# Revit family: ASafe_ASafeHQLtd_HndrlSym_iFlexPedestrianBarrier3Rail
name_source: partatom
category: Railings
revit_build: Autodesk Revit 2018 (Build: 20170223_1515(x64)
units: mm (PartAtom-declared; Revit-internal decimal feet)

## family parameters
Always vertical = No
Cut with Voids When Loaded = No
Shared = No
Work Plane-Based = Yes

## types (8) — shared parameters
AssetType = Fixed
BarrierColour = ASafe_ASafeHQLtd_Memaplex_SignalYellow
BasePlateSize = 180 x 180 mm
BaseplateMaterial = ASafe_ASafeHQLtd_SteelEcoCoating_Black
Category = Ss_25_15_60_35:Handrail systems
ChemicalResistance = Excellent - ISO/TR 10358
Color = Signal yellow
Constituents = Locking pins, Couplings with covers, Fixings
Default Elevation = 1219 mm
Deflection = 320 mm at maximum energy
DurationUnit = year
Duty = Light
FlashPoint = 350°C to 370°C
HandrailHeight = 1050 mm  [stored 3.44488 ft]
HasHygieneSeals = Yes
Height = 1136 mm
IfcExportAs = IfcRailingType
IfcExportType = USERDEFINED
IgnitionTemperature = 350°C to 370°C
ImpactJoules = Dynamically tested to resist an impact of 8,200 Joules from a vehicle impact at 45°
ImpactZone = 450-1100 mm
IsExternal = Yes
LiftingForce = 9 kN
ManufacturerName = A-Safe (HQ) Ltd
ManufacturerURL = https://www.asafe.com
Material = Memaplex
ModelReference = iFlex™ Pedestrian Barrier 3 Rail
MouldColour = ASafe_ASafeHQLtd_Memaplex_SignalYellow
MountingType = Floor fixed
NBSCertification = www.nationalbimlibrary.com/cert/vatznaso
NBSDescription = Handrail system
NBSReference = 25-25-10/135
NominalHeight = 1136 mm
NominalWidth = 130 mm
PostColour = ASafe_ASafeHQLtd_Memaplex_Black
PostHeight = 1136 mm
ProductInformation = https://www.asafe.com
StaticRating = 1015-1016 Ω
Status = UNSET
TemperatureRange = -10°C to 50°C
ThirdPartyCertification = PAS13:2017,TÜV NORD Approved
Toxicity = Not hazardous
Uniclass2015Code = Ss_25_15_60_35
Uniclass2015Title = Handrail systems
Uniclass2015Version = Systems v1.10
Version = 2
WarrantyDurationUnit = year
zero-valued in all types: CrashBarrierHeight, Diameter

## per-type parameters (varying)
| type | AngledEndPost | BIMObjectName | DoubleAngledPost | EndPostAngle | Name | PostAngle | TripleSectionVisibility |
| 4D | Yes | ASafe_ASafeHQLtd_HandrailSystem_iFlexPedestrianBarrier3Rail_4D | Yes | 180.00° | HandrailSystem_iFlexPedestrianBarrier3Rail_4D_ASafeHQLtd | 4D | Yes |
| 90And180Degrees | Yes | ASafe_ASafeHQLtd_HandrailSystem_iFlexPedestrianBarrier3Rail_90And180Degrees | Yes | 180.00° | HandrailSystem_iFlexPedestrianBarrier3Rail_90And180Degrees_ASafeHQLtd | 90° and 180° | No |
| Mid | Yes | ASafe_ASafeHQLtd_HandrailSystem_iFlexPedestrianBarrier3Rail_Mid | No | 180.00° | HandrailSystem_iFlexPedestrianBarrier3Rail_Mid_ASafeHQLtd | 180° | No |
| 157-5Degrees | Yes | ASafe_ASafeHQLtd_HandrailSystem_iFlexPedestrianBarrier3Rail_157-5Degrees | No | 157.50° | HandrailSystem_iFlexPedestrianBarrier3Rail_157-5Degrees_ASafeHQLtd | 157.5° | No |
| 135Degrees | Yes | ASafe_ASafeHQLtd_HandrailSystem_iFlexPedestrianBarrier3Rail_135Degrees | No | 135.00° | HandrailSystem_iFlexPedestrianBarrier3Rail_135Degrees_ASafeHQLtd | 135° | No |
| 112-5Degrees | Yes | ASafe_ASafeHQLtd_HandrailSystem_iFlexPedestrianBarrier3Rail_112-5Degrees | No | 112.50° | HandrailSystem_iFlexPedestrianBarrier3Rail_112-5Degrees_ASafeHQLtd | 112.5° | No |
| 90Degrees | Yes | ASafe_ASafeHQLtd_HandrailSystem_iFlexPedestrianBarrier3Rail_90Degrees | No | 90.00° | HandrailSystem_iFlexPedestrianBarrier3Rail_90Degrees_ASafeHQLtd | 90° | No |
| End | No | ASafe_ASafeHQLtd_HandrailSystem_iFlexPedestrianBarrier3Rail_End | No | 0.00° | HandrailSystem_iFlexPedestrianBarrier3Rail_End_ASafeHQLtd |  | No |

note: [stored X ft] marks values corroborated as IEEE doubles in the binary element streams (Revit-internal decimal feet)

## geometry (parser evidence)
native form markers: Extrusion x1, Sweep x10
no freeform markers — native parametric forms only
